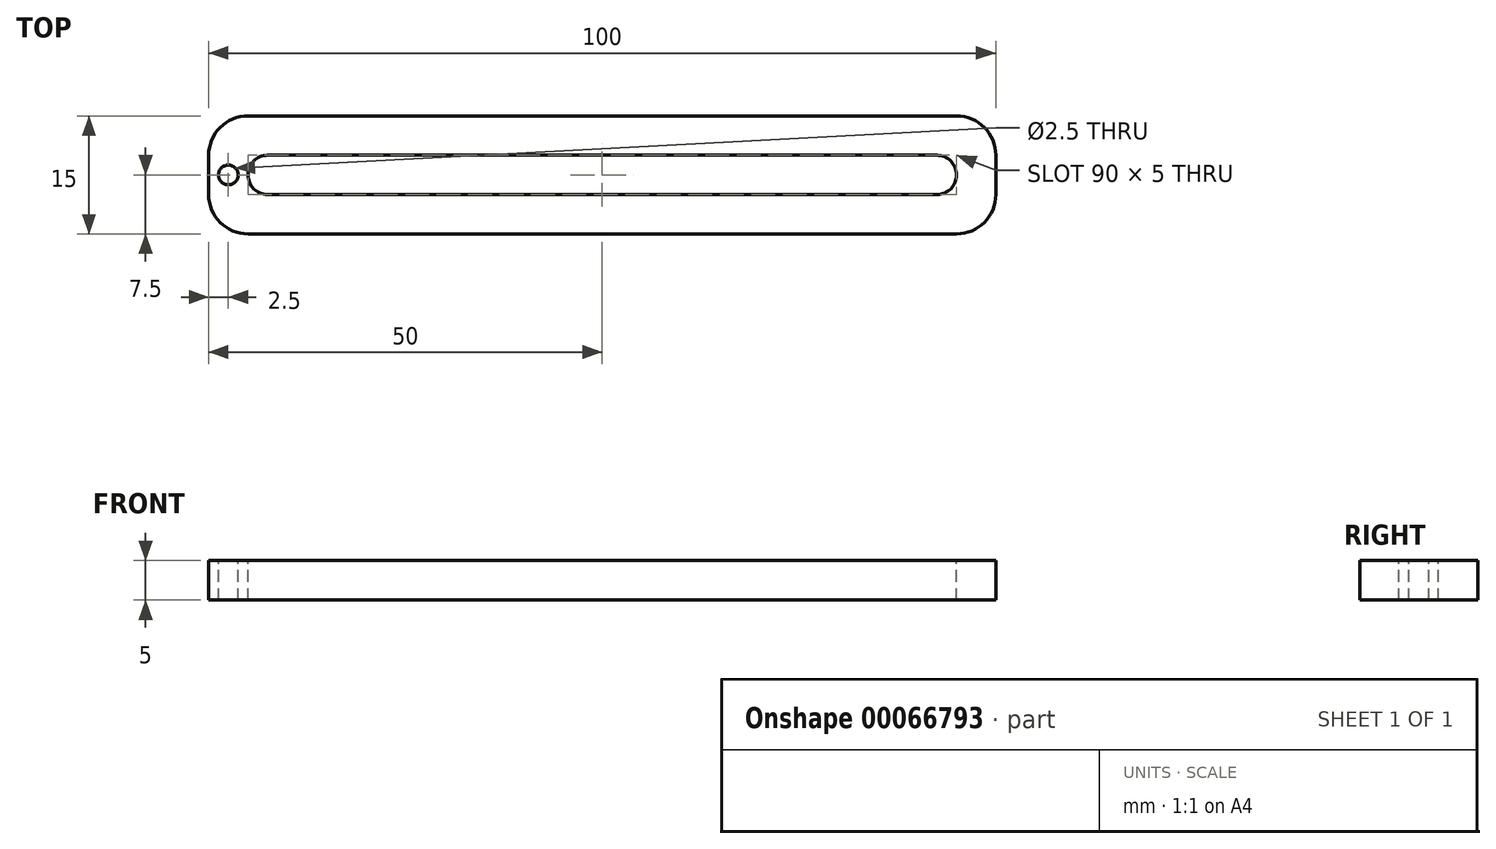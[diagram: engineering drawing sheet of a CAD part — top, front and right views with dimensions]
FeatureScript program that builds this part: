
annotation { "Feature Type Name" : "Feature", "Feature Type Description" : "" }
export const myFeature = defineFeature(function(context is Context, id is Id, definition is map)
    precondition{}
    {
        {
            var Q0;
            Q0=qCreatedBy(makeId("Top.planeOp"),FACE);
            var sketch = newSketch(context, id + "F0", { "sketchPlane" : qUnion([Q0])});
            skLineSegment(sketch, "E0.rect.bottom", {"start": v(45, 7.5) * mm, "end": v(-45, 7.5) * mm});
            skLineSegment(sketch, "E0.rect.top", {"start": v(45, -7.5) * mm, "end": v(-45, -7.5) * mm});
            skLineSegment(sketch, "E0.rect.left", {"start": v(50, 2.5) * mm, "end": v(50, -2.5) * mm});
            skLineSegment(sketch, "E0.rect.right", {"start": v(-50, 2.5) * mm, "end": v(-50, -2.5) * mm});
            skPoint(sketch, "E0.rect.middle", {"position": v(0, 0) * mm});
            skPoint(sketch, "E1.visualSharp", {"position": v(-50, 7.5) * mm});
            skArc(sketch, "E1.filletArc", {"start": v(-45, 7.5) * mm, "mid": v(-48.54, 6.04) * mm, "end": v(-50, 2.5) * mm});
            skPoint(sketch, "E2.visualSharp", {"position": v(-50, -7.5) * mm});
            skArc(sketch, "E2.filletArc", {"start": v(-50, -2.5) * mm, "mid": v(-48.54, -6.04) * mm, "end": v(-45, -7.5) * mm});
            skPoint(sketch, "E3.visualSharp", {"position": v(50, 7.5) * mm});
            skArc(sketch, "E3.filletArc", {"start": v(50, 2.5) * mm, "mid": v(48.54, 6.04) * mm, "end": v(45, 7.5) * mm});
            skPoint(sketch, "E4.visualSharp", {"position": v(50, -7.5) * mm});
            skArc(sketch, "E4.filletArc", {"start": v(45, -7.5) * mm, "mid": v(48.54, -6.04) * mm, "end": v(50, -2.5) * mm});
            skSolve(sketch);
        }
        {
            var Q0;
            Q0=makeQuery(id+"F0.imprint","IMPRINT",FACE,{"disambiguationData":[TD([[makeQuery(id+"F0.imprint","IMPRINT",EDGE,{"derivedFrom":sQuery(id+"F0.wireOp",EDGE,"E0.rect.bottom")}),1.0]])]});
            extrude(context, id + "F1", {"entities" : qUnion([Q0]), "endBound" : BoundingType.SYMMETRIC, "depth" : 5 * mm});
        }
        {
            var Q0;
            Q0=makeQuery(id+"F1.opExtrude","CAP_FACE",FACE,{"disambiguationData":[OSD([sQuery(id+"F0.wireOp",EDGE,"E0.rect.bottom"),sQuery(id+"F0.wireOp",EDGE,"E0.rect.top"),sQuery(id+"F0.wireOp",EDGE,"E0.rect.left"),sQuery(id+"F0.wireOp",EDGE,"E0.rect.right"),sQuery(id+"F0.wireOp",EDGE,"E1.filletArc"),sQuery(id+"F0.wireOp",EDGE,"E2.filletArc"),sQuery(id+"F0.wireOp",EDGE,"E3.filletArc"),sQuery(id+"F0.wireOp",EDGE,"E4.filletArc")])],"isStart":false});
            var sketch = newSketch(context, id + "F2", { "sketchPlane" : qUnion([Q0])});
            skLineSegment(sketch, "E5.rect.bottom", {"start": v(-42.5, 2.5) * mm, "end": v(42.5, 2.5) * mm});
            skLineSegment(sketch, "E5.rect.top", {"start": v(-42.5, -2.5) * mm, "end": v(42.5, -2.5) * mm});
            skLineSegment(sketch, "E5.rect.left", {"start": v(-45, 0) * mm, "end": v(-45, 0) * mm});
            skLineSegment(sketch, "E5.rect.right", {"start": v(45, 0) * mm, "end": v(45, 0) * mm});
            skPoint(sketch, "E5.rect.middle", {"position": v(0, 0) * mm});
            skPoint(sketch, "E6.visualSharp", {"position": v(-45, 2.5) * mm});
            skArc(sketch, "E6.filletArc", {"start": v(-42.5, 2.5) * mm, "mid": v(-44.27, 1.77) * mm, "end": v(-45, 0) * mm});
            skPoint(sketch, "E7.visualSharp", {"position": v(-45, -2.5) * mm});
            skArc(sketch, "E7.filletArc", {"start": v(-45, 0) * mm, "mid": v(-44.27, -1.77) * mm, "end": v(-42.5, -2.5) * mm});
            skPoint(sketch, "E8.visualSharp", {"position": v(45, 2.5) * mm});
            skArc(sketch, "E8.filletArc", {"start": v(45, 0) * mm, "mid": v(44.27, 1.77) * mm, "end": v(42.5, 2.5) * mm});
            skPoint(sketch, "E9.visualSharp", {"position": v(45, -2.5) * mm});
            skArc(sketch, "E9.filletArc", {"start": v(42.5, -2.5) * mm, "mid": v(44.27, -1.77) * mm, "end": v(45, 0) * mm});
            skSolve(sketch);
        }
        {
            var Q0;
            Q0=makeQuery(id+"F2.imprint","IMPRINT",FACE,{"disambiguationData":[TD([[makeQuery(id+"F2.imprint","IMPRINT",EDGE,{"derivedFrom":sQuery(id+"F2.wireOp",EDGE,"E5.rect.bottom")}),-1.0]])]});
            extrude(context, id + "F3", {"entities" : qUnion([Q0]), "operationType" : NewBodyOperationType.REMOVE, "endBound" : BoundingType.THROUGH_ALL, "oppositeDirection" : true, "depth" : 25 * mm});
        }
        {
            var Q0;
            Q0=makeQuery(id+"F1.opExtrude","CAP_FACE",FACE,{"disambiguationData":[OSD([sQuery(id+"F0.wireOp",EDGE,"E0.rect.bottom"),sQuery(id+"F0.wireOp",EDGE,"E0.rect.top"),sQuery(id+"F0.wireOp",EDGE,"E0.rect.left"),sQuery(id+"F0.wireOp",EDGE,"E0.rect.right"),sQuery(id+"F0.wireOp",EDGE,"E1.filletArc"),sQuery(id+"F0.wireOp",EDGE,"E2.filletArc"),sQuery(id+"F0.wireOp",EDGE,"E3.filletArc"),sQuery(id+"F0.wireOp",EDGE,"E4.filletArc")])],"isStart":false});
            var sketch = newSketch(context, id + "F4", { "sketchPlane" : qUnion([Q0])});
            skCircle(sketch, "E10", {"center": v(-47.5, 0) * mm, "radius": 1.25 * mm});
            skSolve(sketch);
        }
        {
            var Q0;
            Q0=makeQuery(id+"F4.imprint","IMPRINT",FACE,{"disambiguationData":[TD([[makeQuery(id+"F4.imprint","IMPRINT",EDGE,{"derivedFrom":sQuery(id+"F4.wireOp",EDGE,"E10")}),1.0]])]});
            extrude(context, id + "F5", {"entities" : qUnion([Q0]), "operationType" : NewBodyOperationType.REMOVE, "endBound" : BoundingType.THROUGH_ALL, "oppositeDirection" : true, "depth" : 25 * mm});
        }
    });
